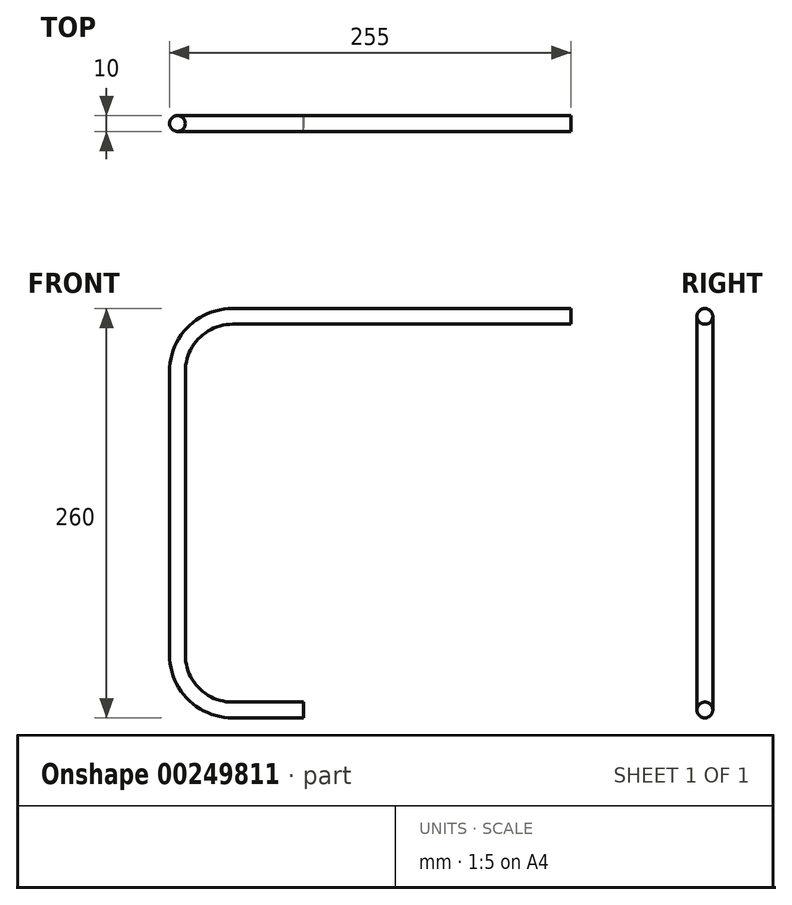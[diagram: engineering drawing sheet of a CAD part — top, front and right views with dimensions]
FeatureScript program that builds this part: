
annotation { "Feature Type Name" : "Feature", "Feature Type Description" : "" }
export const myFeature = defineFeature(function(context is Context, id is Id, definition is map)
    precondition{}
    {
        {
            var Q0;
            Q0=qCreatedBy(makeId("Front.planeOp"),FACE);
            var sketch = newSketch(context, id + "F0", { "sketchPlane" : qUnion([Q0])});
            skLineSegment(sketch, "E0", {"start": v(0, 0) * mm, "end": v(-215, 0) * mm});
            skLineSegment(sketch, "E1", {"start": v(-250, -35) * mm, "end": v(-250, -215) * mm});
            skLineSegment(sketch, "E2", {"start": v(-215, -250) * mm, "end": v(-170, -250) * mm});
            skPoint(sketch, "E3.visualSharp", {"position": v(-250, 0) * mm});
            skArc(sketch, "E3.filletArc", {"start": v(-215, 0) * mm, "mid": v(-239.75, -10.25) * mm, "end": v(-250, -35) * mm});
            skPoint(sketch, "E4.visualSharp", {"position": v(-250, -250) * mm});
            skArc(sketch, "E4.filletArc", {"start": v(-250, -215) * mm, "mid": v(-239.75, -239.75) * mm, "end": v(-215, -250) * mm});
            skSolve(sketch);
        }
        {
            var Q0;
            Q0=qCreatedBy(makeId("Right.planeOp"),FACE);
            var sketch = newSketch(context, id + "F1", { "sketchPlane" : qUnion([Q0])});
            skCircle(sketch, "E5", {"center": v(0, 0) * mm, "radius": 5 * mm});
            skSolve(sketch);
        }
        {
            var Q0;
            Q0=makeQuery(id+"F1.imprint","IMPRINT",FACE,{"disambiguationData":[TD([[makeQuery(id+"F1.imprint","IMPRINT",EDGE,{"derivedFrom":sQuery(id+"F1.wireOp",EDGE,"E5")}),1.0]])]});
            var Q1;
            Q1=sQuery(id+"F0.wireOp",EDGE,"E0");
            var Q2;
            Q2=sQuery(id+"F0.wireOp",EDGE,"E3.filletArc");
            var Q3;
            Q3=sQuery(id+"F0.wireOp",EDGE,"E1");
            var Q4;
            Q4=sQuery(id+"F0.wireOp",EDGE,"E4.filletArc");
            var Q5;
            Q5=sQuery(id+"F0.wireOp",EDGE,"E2");
            sweep(context, id + "F2", {"profiles" : qUnion([Q0]), "path" : qUnion([Q1, Q2, Q3, Q4, Q5])});
        }
    });
